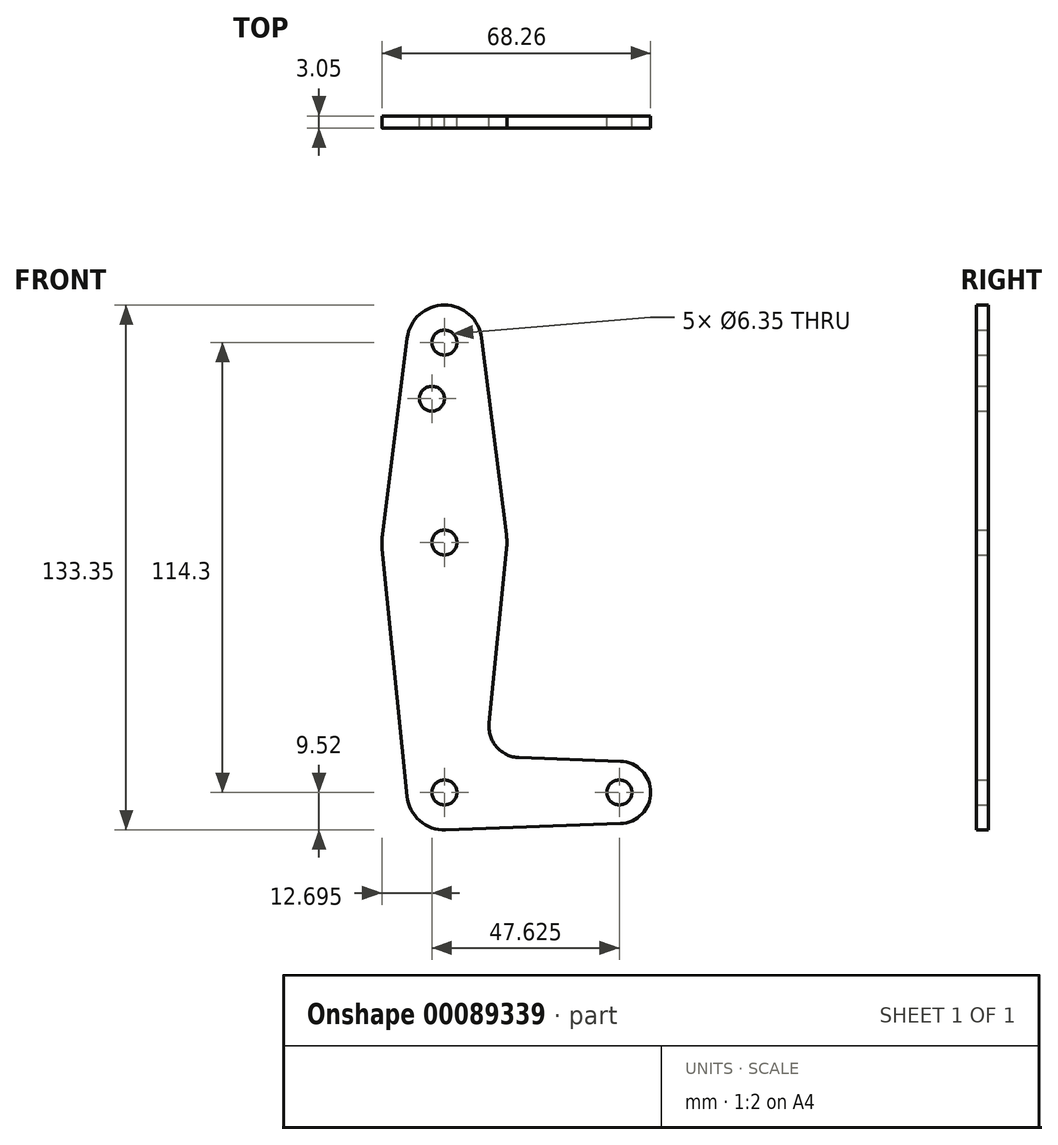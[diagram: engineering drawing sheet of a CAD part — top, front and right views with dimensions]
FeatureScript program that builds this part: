
annotation { "Feature Type Name" : "Feature", "Feature Type Description" : "" }
export const myFeature = defineFeature(function(context is Context, id is Id, definition is map)
    precondition{}
    {
        {
            var Q0;
            Q0=qCreatedBy(makeId("Front.planeOp"),FACE);
            var sketch = newSketch(context, id + "F0", { "sketchPlane" : qUnion([Q0])});
            skCircle(sketch, "E0", {"center": v(0, 63.5) * mm, "radius": 15.88 * mm});
            skCircle(sketch, "E1", {"center": v(0, 0) * mm, "radius": 9.53 * mm});
            skCircle(sketch, "E2", {"center": v(0, 114.3) * mm, "radius": 9.53 * mm});
            skCircle(sketch, "E3", {"center": v(44.45, 0) * mm, "radius": 7.94 * mm});
            skLineSegment(sketch, "E4", {"start": v(9.45, 115.5) * mm, "end": v(15.75, 65.48) * mm});
            skLineSegment(sketch, "E5", {"start": v(-9.45, 115.5) * mm, "end": v(-15.75, 65.48) * mm});
            skLineSegment(sketch, "E6", {"start": v(-15.8, 61.91) * mm, "end": v(-9.48, -0.95) * mm});
            skLineSegment(sketch, "E7", {"start": v(15.8, 61.91) * mm, "end": v(11.34, 17.6) * mm});
            skLineSegment(sketch, "E8", {"start": v(18.97, 8.85) * mm, "end": v(44.73, 7.93) * mm});
            skLineSegment(sketch, "E9", {"start": v(0.34, -9.52) * mm, "end": v(44.73, -7.93) * mm});
            skArc(sketch, "E10", {"start": v(11.34, 17.6) * mm, "mid": v(13.26, 11.57) * mm, "end": v(18.97, 8.85) * mm});
            skCircle(sketch, "E11", {"center": v(0, 0) * mm, "radius": 3.18 * mm});
            skCircle(sketch, "E12", {"center": v(0, 114.3) * mm, "radius": 3.18 * mm});
            skCircle(sketch, "E13", {"center": v(0, 63.5) * mm, "radius": 3.17 * mm});
            skCircle(sketch, "E14", {"center": v(44.45, 0) * mm, "radius": 3.18 * mm});
            skLineSegment(sketch, "E15", {"start": v(0, 114.3) * mm, "end": v(0, 63.5) * mm});
            skCircle(sketch, "E16", {"center": v(-3.17, 100.03) * mm, "radius": 3.18 * mm});
            skSolve(sketch);
        }
        {
            var Q0;
            Q0 = qSketchRegion(id + "F0", true);
            extrude(context, id + "F1", {"entities" : qUnion([Q0]), "depth" : 3.05 * mm});
        }
    });
